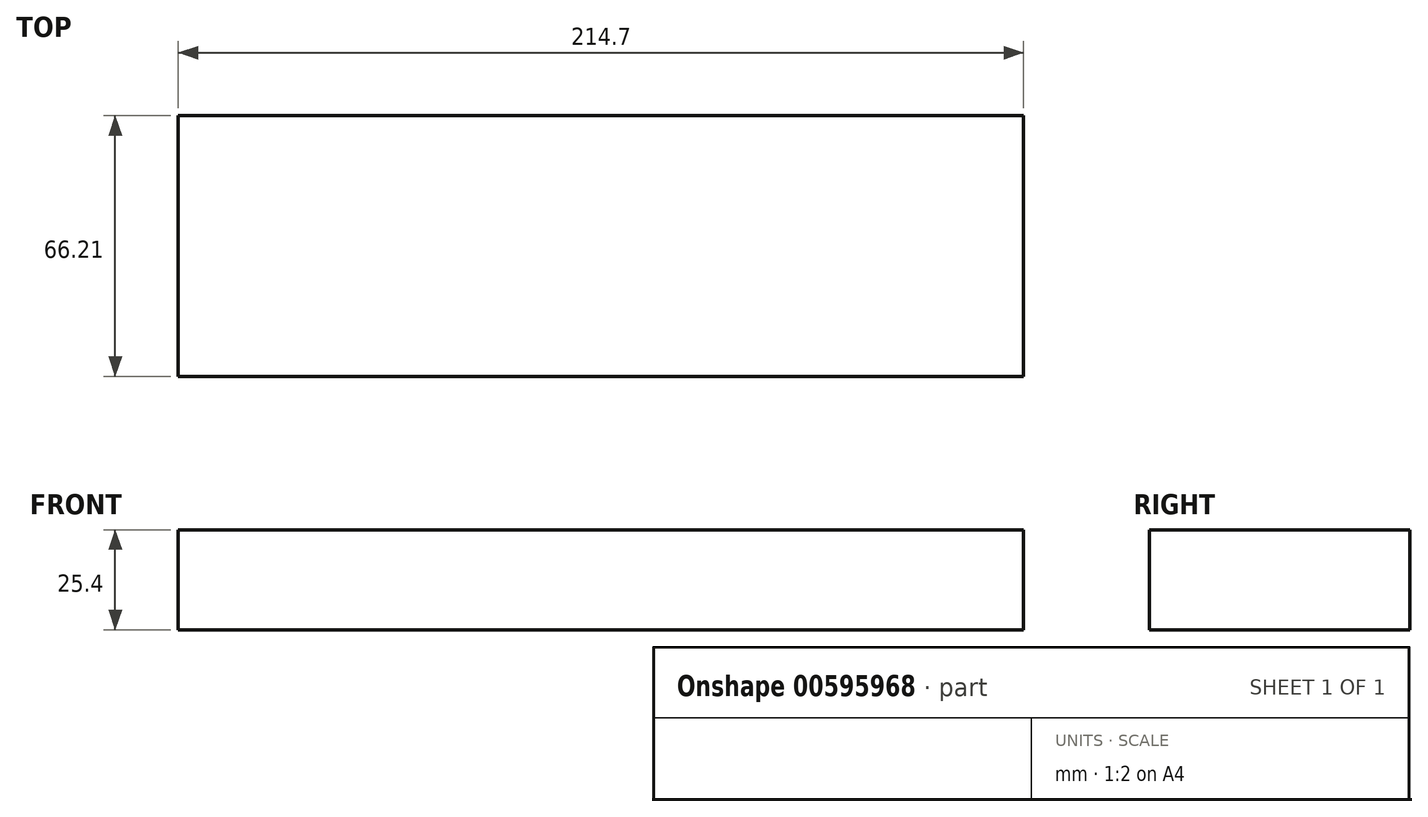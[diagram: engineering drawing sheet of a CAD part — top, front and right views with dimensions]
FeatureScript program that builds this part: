
annotation { "Feature Type Name" : "Feature", "Feature Type Description" : "" }
export const myFeature = defineFeature(function(context is Context, id is Id, definition is map)
    precondition{}
    {
        {
            var Q0;
            Q0=qCreatedBy(makeId("Top.planeOp"),FACE);
            var sketch = newSketch(context, id + "F0", { "sketchPlane" : qUnion([Q0])});
            skLineSegment(sketch, "E0", {"start": v(-191.5, 26.06) * mm, "end": v(23.19, 26.06) * mm});
            skLineSegment(sketch, "E1", {"start": v(23.19, 92.27) * mm, "end": v(23.19, 26.06) * mm});
            skLineSegment(sketch, "E2", {"start": v(23.19, 92.27) * mm, "end": v(-191.5, 92.27) * mm});
            skLineSegment(sketch, "E3", {"start": v(-191.5, 92.27) * mm, "end": v(-191.5, 26.06) * mm});
            skSolve(sketch);
        }
        {
            var Q0;
            Q0 = qSketchRegion(id + "F0", true);
            extrude(context, id + "F1", {"entities" : qUnion([Q0]), "depth" : 25.4 * mm, "offsetDistance" : 25.4 * mm});
        }
    });
